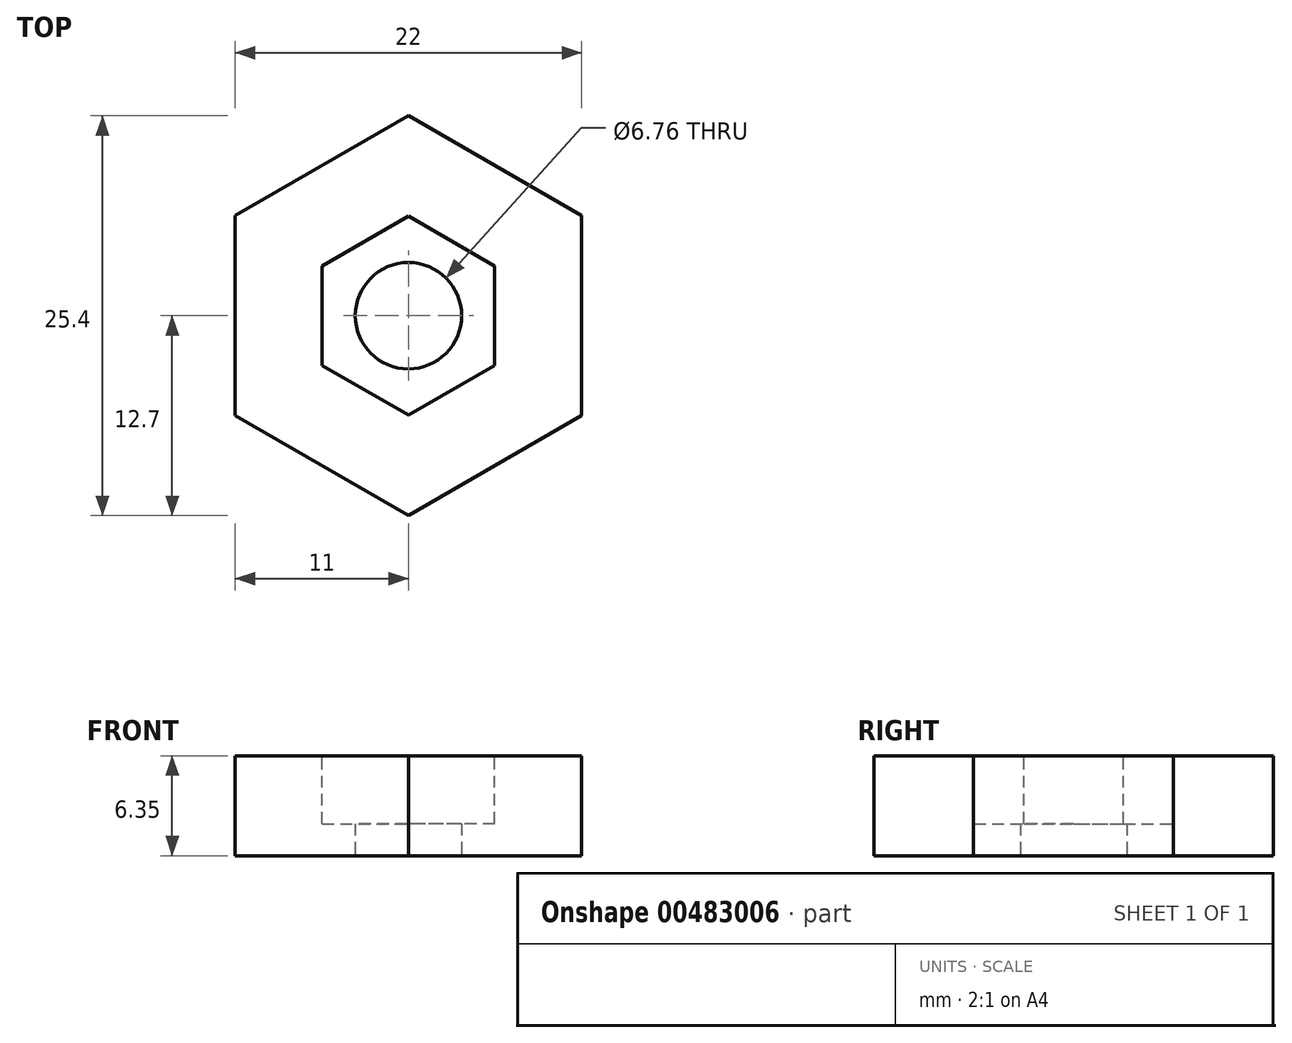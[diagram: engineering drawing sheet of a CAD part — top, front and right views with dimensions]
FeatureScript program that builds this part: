
annotation { "Feature Type Name" : "Feature", "Feature Type Description" : "" }
export const myFeature = defineFeature(function(context is Context, id is Id, definition is map)
    precondition{}
    {
        {
            var Q0;
            Q0=qCreatedBy(makeId("Top.planeOp"),FACE);
            var sketch = newSketch(context, id + "F0", { "sketchPlane" : qUnion([Q0])});
            skCircle(sketch, "E0.cCircle", {"center": v(0, 0) * mm, "radius": 12.7 * mm, "construction": true});
            skLineSegment(sketch, "E0.0", {"start": v(11, -6.35) * mm, "end": v(0, -12.7) * mm});
            skLineSegment(sketch, "E0.1", {"start": v(0, -12.7) * mm, "end": v(-11, -6.35) * mm});
            skLineSegment(sketch, "E0.2", {"start": v(-11, -6.35) * mm, "end": v(-11, 6.35) * mm});
            skLineSegment(sketch, "E0.3", {"start": v(-11, 6.35) * mm, "end": v(0, 12.7) * mm});
            skLineSegment(sketch, "E0.4", {"start": v(0, 12.7) * mm, "end": v(11, 6.35) * mm});
            skLineSegment(sketch, "E0.5", {"start": v(11, 6.35) * mm, "end": v(11, -6.35) * mm});
            skCircle(sketch, "E1.cCircle", {"center": v(0, 0) * mm, "radius": 5.47 * mm, "construction": true});
            skLineSegment(sketch, "E1.0", {"start": v(5.47, 3.16) * mm, "end": v(5.47, -3.16) * mm});
            skLineSegment(sketch, "E1.1", {"start": v(5.47, -3.16) * mm, "end": v(0, -6.32) * mm});
            skLineSegment(sketch, "E1.2", {"start": v(0, -6.32) * mm, "end": v(-5.47, -3.16) * mm});
            skLineSegment(sketch, "E1.3", {"start": v(-5.47, -3.16) * mm, "end": v(-5.47, 3.16) * mm});
            skLineSegment(sketch, "E1.4", {"start": v(-5.47, 3.16) * mm, "end": v(0, 6.32) * mm});
            skLineSegment(sketch, "E1.5", {"start": v(0, 6.32) * mm, "end": v(5.47, 3.16) * mm});
            skPoint(sketch, "E1.0.midPoint", {"position": v(5.47, 0) * mm});
            skCircle(sketch, "E2", {"center": v(0, 0) * mm, "radius": 3.24 * mm});
            skSolve(sketch);
        }
        {
            var Q0;
            Q0=makeQuery(id+"F0.imprint","IMPRINT",FACE,{"disambiguationData":[TD([[makeQuery(id+"F0.imprint","IMPRINT",EDGE,{"derivedFrom":sQuery(id+"F0.wireOp",EDGE,"E0.0")}),-1.0]])]});
            var Q1;
            Q1=makeQuery(id+"F0.imprint","IMPRINT",FACE,{"disambiguationData":[TD([[makeQuery(id+"F0.imprint","IMPRINT",EDGE,{"derivedFrom":sQuery(id+"F0.wireOp",EDGE,"E1.0")}),-1.0]])]});
            var Q2;
            Q2=makeQuery(id+"F0.imprint","IMPRINT",FACE,{"disambiguationData":[TD([[makeQuery(id+"F0.imprint","IMPRINT",EDGE,{"derivedFrom":sQuery(id+"F0.wireOp",EDGE,"E2")}),1.0]])]});
            extrude(context, id + "F1", {"entities" : qUnion([Q0, Q1, Q2]), "depth" : 6.35 * mm});
        }
        {
            var Q0;
            Q0=makeQuery(id+"F1.opExtrude","CAP_FACE",FACE,{"disambiguationData":[OSD([sQuery(id+"F0.wireOp",EDGE,"E0.0"),sQuery(id+"F0.wireOp",EDGE,"E0.1"),sQuery(id+"F0.wireOp",EDGE,"E0.2"),sQuery(id+"F0.wireOp",EDGE,"E0.3"),sQuery(id+"F0.wireOp",EDGE,"E0.4"),sQuery(id+"F0.wireOp",EDGE,"E0.5")])],"isStart":false});
            var sketch = newSketch(context, id + "F2", { "sketchPlane" : qUnion([Q0])});
            skLineSegment(sketch, "E3.0", {"start": v(-5.47, 3.16) * mm, "end": v(0, 6.32) * mm});
            skLineSegment(sketch, "E4.0", {"start": v(-5.47, -3.16) * mm, "end": v(-5.47, 3.16) * mm});
            skLineSegment(sketch, "E4.1", {"start": v(0, -6.32) * mm, "end": v(-5.47, -3.16) * mm});
            skLineSegment(sketch, "E5.0", {"start": v(5.47, -3.16) * mm, "end": v(0, -6.32) * mm});
            skLineSegment(sketch, "E5.1", {"start": v(5.47, 3.16) * mm, "end": v(5.47, -3.16) * mm});
            skLineSegment(sketch, "E5.2", {"start": v(0, 6.32) * mm, "end": v(5.47, 3.16) * mm});
            skSolve(sketch);
        }
        {
            var Q0;
            Q0=makeQuery(id+"F2.imprint","IMPRINT",FACE,{"disambiguationData":[TD([[makeQuery(id+"F2.imprint","IMPRINT",EDGE,{"derivedFrom":sQuery(id+"F2.wireOp",EDGE,"E3.0")}),-1.0]])]});
            extrude(context, id + "F3", {"entities" : qUnion([Q0]), "operationType" : NewBodyOperationType.REMOVE, "oppositeDirection" : true, "depth" : 4.32 * mm});
        }
        {
            var Q0;
            Q0=sQuery(id+"F0.wireOp",VERTEX,"E1.cCircle.center");
            var Q1;
            Q1=makeQuery(id+"F1.opExtrude","SWEPT_BODY",BODY,{"disambiguationData":[OSD([sQuery(id+"F0.wireOp",EDGE,"E0.0"),sQuery(id+"F0.wireOp",EDGE,"E0.1"),sQuery(id+"F0.wireOp",EDGE,"E0.2"),sQuery(id+"F0.wireOp",EDGE,"E0.3"),sQuery(id+"F0.wireOp",EDGE,"E0.4"),sQuery(id+"F0.wireOp",EDGE,"E0.5")])]});
            hole(context, id + "F4", {"style" : HoleStyle.SIMPLE, "endStyle" : HoleEndStyle.THROUGH, "oppositeDirection" : true, "standardTappedOrClearance" : lookupTablePath({ "standard" : "ANSI", "fit" : "Normal (ASME)", "size" : "1/4", "type" : "Clearance" }), "standardBlindInLast" : lookupTablePath({ "fit" : "Free", "standard" : "ANSI", "size" : "1/4", "type" : "Clearance" }), "holeDiameter" : 6.76 * mm, "isTappedThrough" : true, "tappedDepth" : 12.7 * mm, "tapClearance" : 3, "locations" : qUnion([Q0]), "scope" : qUnion([Q1])});
        }
    });
